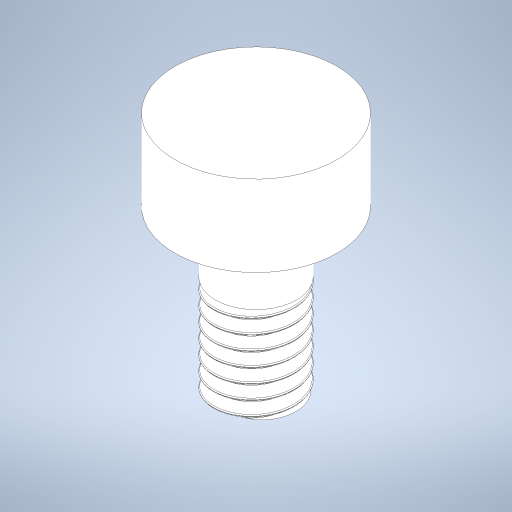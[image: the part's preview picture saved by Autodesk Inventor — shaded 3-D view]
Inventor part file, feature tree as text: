
AUTODESK INVENTOR PART (.ipt)
format: ipt  version: 2023 (Build 270158000, 158)  size: 719,872 bytes
history: native  units: in
note: dims shown in document units (in); Inventor stores cm internally (conversion verified against a paired STEP export)
features: sketch x4, revolve x3, thread x1, helix x1
ambient origin geometry x8: Origin, YZ Plane, XZ Plane, XY Plane, X Axis, Y Axis, Z Axis, Center Point
bodies: Solid1 (feature_tree), Solid3 (feature_tree)
feature tree (9):
  revolve  "Revolution1"  [1 undecoded]
  thread  "Thread2"  [1 undecoded]
  revolve  "Revolution4"  Angle=90.0deg
  revolve  "Revolution5"  [1 undecoded]
  helix  "Coil2"  [1 undecoded]
  sketch  "Sketch1"  dims[d0=0.315in d1=0.0787in d2=0.1575in]
  sketch  "Sketch5"  dims[d3=0.1575in d4=90.0deg]
  sketch  "Sketch6"  dims[d14=0.3779in d26=0.1969in d27=0.0in d28=0.3779in d29=0.0044in d30=0.0044in]
  sketch  "Sketch7"  dims[d33=0.0276in d35=0.3779in d37=0.0in d38=0.0in d39=0.0276in d40=0.252in d41=0.3937in d42=0.0in d43=0.0in d44=0.0in d45=0.0in d46=0.0in]
note: 4 required parameter values undecoded (feature->parameter linkage not recoverable at this tier; creation-order binding heuristic only, values carry confidence <= 0.55)